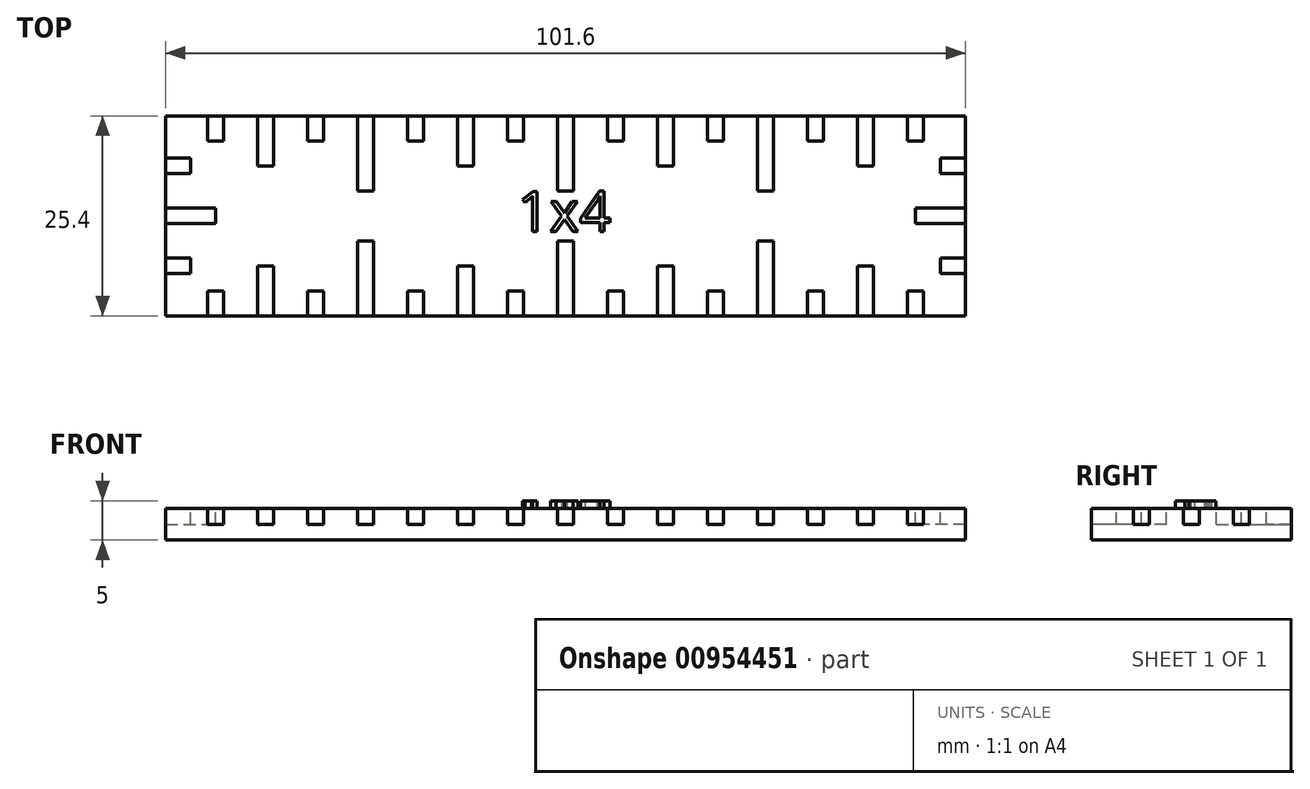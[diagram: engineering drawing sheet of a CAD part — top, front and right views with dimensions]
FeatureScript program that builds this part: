
annotation { "Feature Type Name" : "Feature", "Feature Type Description" : "" }
export const myFeature = defineFeature(function(context is Context, id is Id, definition is map)
    precondition{}
    {
        {
            var Q0;
            Q0=qCreatedBy(makeId("Top.planeOp"),FACE);
            var sketch = newSketch(context, id + "F0", { "sketchPlane" : qUnion([Q0])});
            skLineSegment(sketch, "E0.bottom", {"start": v(-50.8, 12.7) * mm, "end": v(50.8, 12.7) * mm});
            skLineSegment(sketch, "E0.top", {"start": v(-50.8, -12.7) * mm, "end": v(50.8, -12.7) * mm});
            skLineSegment(sketch, "E0.left", {"start": v(-50.8, 12.7) * mm, "end": v(-50.8, -12.7) * mm});
            skLineSegment(sketch, "E0.right", {"start": v(50.8, 12.7) * mm, "end": v(50.8, -12.7) * mm});
            skPoint(sketch, "E0.middle", {"position": v(0, 0) * mm});
            skSolve(sketch);
        }
        {
            var Q0;
            Q0=makeQuery(id+"F0.imprint","IMPRINT",FACE,{"disambiguationData":[TD([[makeQuery(id+"F0.imprint","IMPRINT",EDGE,{"derivedFrom":sQuery(id+"F0.wireOp",EDGE,"E0.bottom")}),-1.0]])]});
            extrude(context, id + "F1", {"entities" : qUnion([Q0]), "depth" : 4 * mm, "offsetDistance" : 25 * mm});
        }
        {
            var Q0;
            Q0=makeQuery(id+"F1.opExtrude","CAP_FACE",FACE,{"disambiguationData":[OSD([sQuery(id+"F0.wireOp",EDGE,"E0.bottom"),sQuery(id+"F0.wireOp",EDGE,"E0.top"),sQuery(id+"F0.wireOp",EDGE,"E0.left"),sQuery(id+"F0.wireOp",EDGE,"E0.right")])],"isStart":false});
            var sketch = newSketch(context, id + "F2", { "sketchPlane" : qUnion([Q0])});
            skLineSegment(sketch, "E1.bottom", {"start": v(-1, -3.17) * mm, "end": v(1, -3.17) * mm});
            skLineSegment(sketch, "E1.top", {"start": v(-1, -22.23) * mm, "end": v(1, -22.23) * mm});
            skLineSegment(sketch, "E1.left", {"start": v(-1, -3.17) * mm, "end": v(-1, -22.23) * mm});
            skLineSegment(sketch, "E1.right", {"start": v(1, -3.17) * mm, "end": v(1, -22.23) * mm});
            skPoint(sketch, "E1.middle", {"position": v(0, -12.7) * mm});
            skLineSegment(sketch, "E2.bottom", {"start": v(5.35, -9.53) * mm, "end": v(7.35, -9.53) * mm});
            skLineSegment(sketch, "E2.top", {"start": v(5.35, -15.88) * mm, "end": v(7.35, -15.88) * mm});
            skLineSegment(sketch, "E2.left", {"start": v(5.35, -9.53) * mm, "end": v(5.35, -15.88) * mm});
            skLineSegment(sketch, "E2.right", {"start": v(7.35, -9.53) * mm, "end": v(7.35, -15.88) * mm});
            skPoint(sketch, "E2.middle", {"position": v(6.35, -12.7) * mm});
            skLineSegment(sketch, "E3.bottom", {"start": v(-7.35, -9.53) * mm, "end": v(-5.35, -9.53) * mm});
            skLineSegment(sketch, "E3.top", {"start": v(-7.35, -15.88) * mm, "end": v(-5.35, -15.88) * mm});
            skLineSegment(sketch, "E3.left", {"start": v(-7.35, -9.53) * mm, "end": v(-7.35, -15.88) * mm});
            skLineSegment(sketch, "E3.right", {"start": v(-5.35, -9.53) * mm, "end": v(-5.35, -15.88) * mm});
            skPoint(sketch, "E3.middle", {"position": v(-6.35, -12.7) * mm});
            skLineSegment(sketch, "E4.bottom", {"start": v(-57.15, -1) * mm, "end": v(-57.15, 1) * mm});
            skLineSegment(sketch, "E4.top", {"start": v(-44.45, -1) * mm, "end": v(-44.45, 1) * mm});
            skLineSegment(sketch, "E4.left", {"start": v(-57.15, -1) * mm, "end": v(-44.45, -1) * mm});
            skLineSegment(sketch, "E4.right", {"start": v(-57.15, 1) * mm, "end": v(-44.45, 1) * mm});
            skPoint(sketch, "E4.middle", {"position": v(-50.8, 0) * mm});
            skLineSegment(sketch, "E5.bottom", {"start": v(-53.98, 5.35) * mm, "end": v(-53.98, 7.35) * mm});
            skLineSegment(sketch, "E5.top", {"start": v(-47.63, 5.35) * mm, "end": v(-47.63, 7.35) * mm});
            skLineSegment(sketch, "E5.left", {"start": v(-53.98, 5.35) * mm, "end": v(-47.63, 5.35) * mm});
            skLineSegment(sketch, "E5.right", {"start": v(-53.98, 7.35) * mm, "end": v(-47.63, 7.35) * mm});
            skPoint(sketch, "E5.middle", {"position": v(-50.8, 6.35) * mm});
            skLineSegment(sketch, "E6.bottom", {"start": v(-53.98, -7.35) * mm, "end": v(-53.98, -5.35) * mm});
            skLineSegment(sketch, "E6.top", {"start": v(-47.63, -7.35) * mm, "end": v(-47.63, -5.35) * mm});
            skLineSegment(sketch, "E6.left", {"start": v(-53.98, -7.35) * mm, "end": v(-47.63, -7.35) * mm});
            skLineSegment(sketch, "E6.right", {"start": v(-53.98, -5.35) * mm, "end": v(-47.63, -5.35) * mm});
            skPoint(sketch, "E6.middle", {"position": v(-50.8, -6.35) * mm});
            skLineSegment(sketch, "E7.bottom", {"start": v(1, 3.17) * mm, "end": v(-1, 3.17) * mm});
            skLineSegment(sketch, "E7.top", {"start": v(1, 22.22) * mm, "end": v(-1, 22.22) * mm});
            skLineSegment(sketch, "E7.left", {"start": v(1, 3.17) * mm, "end": v(1, 22.22) * mm});
            skLineSegment(sketch, "E7.right", {"start": v(-1, 3.17) * mm, "end": v(-1, 22.22) * mm});
            skPoint(sketch, "E7.middle", {"position": v(0, 12.7) * mm});
            skLineSegment(sketch, "E8.bottom", {"start": v(-5.35, 9.53) * mm, "end": v(-7.35, 9.53) * mm});
            skLineSegment(sketch, "E8.top", {"start": v(-5.35, 15.88) * mm, "end": v(-7.35, 15.88) * mm});
            skLineSegment(sketch, "E8.left", {"start": v(-5.35, 9.53) * mm, "end": v(-5.35, 15.88) * mm});
            skLineSegment(sketch, "E8.right", {"start": v(-7.35, 9.53) * mm, "end": v(-7.35, 15.88) * mm});
            skPoint(sketch, "E8.middle", {"position": v(-6.35, 12.7) * mm});
            skLineSegment(sketch, "E9.bottom", {"start": v(7.35, 9.52) * mm, "end": v(5.35, 9.52) * mm});
            skLineSegment(sketch, "E9.top", {"start": v(7.35, 15.88) * mm, "end": v(5.35, 15.88) * mm});
            skLineSegment(sketch, "E9.left", {"start": v(7.35, 9.52) * mm, "end": v(7.35, 15.88) * mm});
            skLineSegment(sketch, "E9.right", {"start": v(5.35, 9.52) * mm, "end": v(5.35, 15.88) * mm});
            skPoint(sketch, "E9.middle", {"position": v(6.35, 12.7) * mm});
            skLineSegment(sketch, "E10.bottom", {"start": v(57.15, 1) * mm, "end": v(57.15, -1) * mm});
            skLineSegment(sketch, "E10.top", {"start": v(44.45, 1) * mm, "end": v(44.45, -1) * mm});
            skLineSegment(sketch, "E10.left", {"start": v(57.15, 1) * mm, "end": v(44.45, 1) * mm});
            skLineSegment(sketch, "E10.right", {"start": v(57.15, -1) * mm, "end": v(44.45, -1) * mm});
            skPoint(sketch, "E10.middle", {"position": v(50.8, 0) * mm});
            skLineSegment(sketch, "E11.bottom", {"start": v(53.98, -5.35) * mm, "end": v(53.98, -7.35) * mm});
            skLineSegment(sketch, "E11.top", {"start": v(47.63, -5.35) * mm, "end": v(47.63, -7.35) * mm});
            skLineSegment(sketch, "E11.left", {"start": v(53.98, -5.35) * mm, "end": v(47.63, -5.35) * mm});
            skLineSegment(sketch, "E11.right", {"start": v(53.98, -7.35) * mm, "end": v(47.63, -7.35) * mm});
            skPoint(sketch, "E11.middle", {"position": v(50.8, -6.35) * mm});
            skLineSegment(sketch, "E12.bottom", {"start": v(53.98, 7.35) * mm, "end": v(53.98, 5.35) * mm});
            skLineSegment(sketch, "E12.top", {"start": v(47.63, 7.35) * mm, "end": v(47.63, 5.35) * mm});
            skLineSegment(sketch, "E12.left", {"start": v(53.98, 7.35) * mm, "end": v(47.63, 7.35) * mm});
            skLineSegment(sketch, "E12.right", {"start": v(53.98, 5.35) * mm, "end": v(47.63, 5.35) * mm});
            skPoint(sketch, "E12.middle", {"position": v(50.8, 6.35) * mm});
            skLineSegment(sketch, "E13.bottom", {"start": v(-11.7, 6.35) * mm, "end": v(-13.7, 6.35) * mm});
            skLineSegment(sketch, "E13.top", {"start": v(-11.7, 19.05) * mm, "end": v(-13.7, 19.05) * mm});
            skLineSegment(sketch, "E13.left", {"start": v(-11.7, 6.35) * mm, "end": v(-11.7, 19.05) * mm});
            skLineSegment(sketch, "E13.right", {"start": v(-13.7, 6.35) * mm, "end": v(-13.7, 19.05) * mm});
            skPoint(sketch, "E13.middle", {"position": v(-12.7, 12.7) * mm});
            skLineSegment(sketch, "E14.bottom", {"start": v(-18.05, 9.53) * mm, "end": v(-20.05, 9.53) * mm});
            skLineSegment(sketch, "E14.top", {"start": v(-18.05, 15.88) * mm, "end": v(-20.05, 15.88) * mm});
            skLineSegment(sketch, "E14.left", {"start": v(-18.05, 9.53) * mm, "end": v(-18.05, 15.88) * mm});
            skLineSegment(sketch, "E14.right", {"start": v(-20.05, 9.53) * mm, "end": v(-20.05, 15.88) * mm});
            skPoint(sketch, "E14.middle", {"position": v(-19.05, 12.7) * mm});
            skLineSegment(sketch, "E15.bottom", {"start": v(-11.7, -19.05) * mm, "end": v(-13.7, -19.05) * mm});
            skLineSegment(sketch, "E15.top", {"start": v(-11.7, -6.35) * mm, "end": v(-13.7, -6.35) * mm});
            skLineSegment(sketch, "E15.left", {"start": v(-11.7, -19.05) * mm, "end": v(-11.7, -6.35) * mm});
            skLineSegment(sketch, "E15.right", {"start": v(-13.7, -19.05) * mm, "end": v(-13.7, -6.35) * mm});
            skPoint(sketch, "E15.middle", {"position": v(-12.7, -12.7) * mm});
            skLineSegment(sketch, "E16.bottom", {"start": v(-18.05, -15.88) * mm, "end": v(-20.05, -15.88) * mm});
            skLineSegment(sketch, "E16.top", {"start": v(-18.05, -9.53) * mm, "end": v(-20.05, -9.53) * mm});
            skLineSegment(sketch, "E16.left", {"start": v(-18.05, -15.88) * mm, "end": v(-18.05, -9.53) * mm});
            skLineSegment(sketch, "E16.right", {"start": v(-20.05, -15.88) * mm, "end": v(-20.05, -9.53) * mm});
            skPoint(sketch, "E16.middle", {"position": v(-19.05, -12.7) * mm});
            skLineSegment(sketch, "E17.bottom", {"start": v(-5.35, -15.88) * mm, "end": v(-7.35, -15.88) * mm});
            skLineSegment(sketch, "E17.top", {"start": v(-5.35, -9.53) * mm, "end": v(-7.35, -9.53) * mm});
            skLineSegment(sketch, "E17.left", {"start": v(-5.35, -15.88) * mm, "end": v(-5.35, -9.53) * mm});
            skLineSegment(sketch, "E17.right", {"start": v(-7.35, -15.88) * mm, "end": v(-7.35, -9.53) * mm});
            skLineSegment(sketch, "E18.bottom", {"start": v(11.7, -6.35) * mm, "end": v(13.7, -6.35) * mm});
            skLineSegment(sketch, "E18.top", {"start": v(11.7, -19.05) * mm, "end": v(13.7, -19.05) * mm});
            skLineSegment(sketch, "E18.left", {"start": v(11.7, -6.35) * mm, "end": v(11.7, -19.05) * mm});
            skLineSegment(sketch, "E18.right", {"start": v(13.7, -6.35) * mm, "end": v(13.7, -19.05) * mm});
            skPoint(sketch, "E18.middle", {"position": v(12.7, -12.7) * mm});
            skLineSegment(sketch, "E19.bottom", {"start": v(18.05, -9.53) * mm, "end": v(20.05, -9.53) * mm});
            skLineSegment(sketch, "E19.top", {"start": v(18.05, -15.88) * mm, "end": v(20.05, -15.88) * mm});
            skLineSegment(sketch, "E19.left", {"start": v(18.05, -9.53) * mm, "end": v(18.05, -15.88) * mm});
            skLineSegment(sketch, "E19.right", {"start": v(20.05, -9.53) * mm, "end": v(20.05, -15.88) * mm});
            skPoint(sketch, "E19.middle", {"position": v(19.05, -12.7) * mm});
            skLineSegment(sketch, "E20.bottom", {"start": v(11.7, 19.05) * mm, "end": v(13.7, 19.05) * mm});
            skLineSegment(sketch, "E20.top", {"start": v(11.7, 6.35) * mm, "end": v(13.7, 6.35) * mm});
            skLineSegment(sketch, "E20.left", {"start": v(11.7, 19.05) * mm, "end": v(11.7, 6.35) * mm});
            skLineSegment(sketch, "E20.right", {"start": v(13.7, 19.05) * mm, "end": v(13.7, 6.35) * mm});
            skPoint(sketch, "E20.middle", {"position": v(12.7, 12.7) * mm});
            skLineSegment(sketch, "E21.bottom", {"start": v(18.05, 15.88) * mm, "end": v(20.05, 15.88) * mm});
            skLineSegment(sketch, "E21.top", {"start": v(18.05, 9.53) * mm, "end": v(20.05, 9.53) * mm});
            skLineSegment(sketch, "E21.left", {"start": v(18.05, 15.88) * mm, "end": v(18.05, 9.53) * mm});
            skLineSegment(sketch, "E21.right", {"start": v(20.05, 15.88) * mm, "end": v(20.05, 9.53) * mm});
            skPoint(sketch, "E21.middle", {"position": v(19.05, 12.7) * mm});
            skLineSegment(sketch, "E22.bottom", {"start": v(5.35, 15.88) * mm, "end": v(7.35, 15.88) * mm});
            skLineSegment(sketch, "E22.top", {"start": v(5.35, 9.53) * mm, "end": v(7.35, 9.53) * mm});
            skLineSegment(sketch, "E22.left", {"start": v(5.35, 15.88) * mm, "end": v(5.35, 9.53) * mm});
            skLineSegment(sketch, "E22.right", {"start": v(7.35, 15.88) * mm, "end": v(7.35, 9.53) * mm});
            skLineSegment(sketch, "E23.bottom", {"start": v(26.4, 3.17) * mm, "end": v(24.4, 3.17) * mm});
            skLineSegment(sketch, "E23.top", {"start": v(26.4, 22.22) * mm, "end": v(24.4, 22.22) * mm});
            skLineSegment(sketch, "E23.left", {"start": v(26.4, 3.17) * mm, "end": v(26.4, 22.22) * mm});
            skLineSegment(sketch, "E23.right", {"start": v(24.4, 3.17) * mm, "end": v(24.4, 22.22) * mm});
            skPoint(sketch, "E23.middle", {"position": v(25.4, 12.7) * mm});
            skLineSegment(sketch, "E24.bottom", {"start": v(20.05, 9.52) * mm, "end": v(18.05, 9.52) * mm});
            skLineSegment(sketch, "E24.top", {"start": v(20.05, 15.87) * mm, "end": v(18.05, 15.87) * mm});
            skLineSegment(sketch, "E24.left", {"start": v(20.05, 9.52) * mm, "end": v(20.05, 15.87) * mm});
            skLineSegment(sketch, "E24.right", {"start": v(18.05, 9.52) * mm, "end": v(18.05, 15.87) * mm});
            skLineSegment(sketch, "E25.bottom", {"start": v(32.75, 9.52) * mm, "end": v(30.75, 9.52) * mm});
            skLineSegment(sketch, "E25.top", {"start": v(32.75, 15.87) * mm, "end": v(30.75, 15.87) * mm});
            skLineSegment(sketch, "E25.left", {"start": v(32.75, 9.52) * mm, "end": v(32.75, 15.87) * mm});
            skLineSegment(sketch, "E25.right", {"start": v(30.75, 9.52) * mm, "end": v(30.75, 15.87) * mm});
            skPoint(sketch, "E25.middle", {"position": v(31.75, 12.7) * mm});
            skLineSegment(sketch, "E26.bottom", {"start": v(20.05, 9.53) * mm, "end": v(18.05, 9.53) * mm});
            skLineSegment(sketch, "E26.top", {"start": v(20.05, 15.88) * mm, "end": v(18.05, 15.88) * mm});
            skLineSegment(sketch, "E26.left", {"start": v(20.05, 9.53) * mm, "end": v(20.05, 15.88) * mm});
            skLineSegment(sketch, "E26.right", {"start": v(18.05, 9.53) * mm, "end": v(18.05, 15.88) * mm});
            skLineSegment(sketch, "E27.bottom", {"start": v(37.1, 19.05) * mm, "end": v(39.1, 19.05) * mm});
            skLineSegment(sketch, "E27.top", {"start": v(37.1, 6.35) * mm, "end": v(39.1, 6.35) * mm});
            skLineSegment(sketch, "E27.left", {"start": v(37.1, 19.05) * mm, "end": v(37.1, 6.35) * mm});
            skLineSegment(sketch, "E27.right", {"start": v(39.1, 19.05) * mm, "end": v(39.1, 6.35) * mm});
            skPoint(sketch, "E27.middle", {"position": v(38.1, 12.7) * mm});
            skLineSegment(sketch, "E28.bottom", {"start": v(43.45, 15.87) * mm, "end": v(45.45, 15.87) * mm});
            skLineSegment(sketch, "E28.top", {"start": v(43.45, 9.52) * mm, "end": v(45.45, 9.52) * mm});
            skLineSegment(sketch, "E28.left", {"start": v(43.45, 15.87) * mm, "end": v(43.45, 9.52) * mm});
            skLineSegment(sketch, "E28.right", {"start": v(45.45, 15.87) * mm, "end": v(45.45, 9.52) * mm});
            skPoint(sketch, "E28.middle", {"position": v(44.45, 12.7) * mm});
            skLineSegment(sketch, "E29.bottom", {"start": v(30.75, 15.87) * mm, "end": v(32.75, 15.87) * mm});
            skLineSegment(sketch, "E29.top", {"start": v(30.75, 9.52) * mm, "end": v(32.75, 9.52) * mm});
            skLineSegment(sketch, "E29.left", {"start": v(30.75, 15.87) * mm, "end": v(30.75, 9.52) * mm});
            skLineSegment(sketch, "E29.right", {"start": v(32.75, 15.87) * mm, "end": v(32.75, 9.52) * mm});
            skLineSegment(sketch, "E30.bottom", {"start": v(26.4, -22.22) * mm, "end": v(24.4, -22.22) * mm});
            skLineSegment(sketch, "E30.top", {"start": v(26.4, -3.17) * mm, "end": v(24.4, -3.17) * mm});
            skLineSegment(sketch, "E30.left", {"start": v(26.4, -22.22) * mm, "end": v(26.4, -3.17) * mm});
            skLineSegment(sketch, "E30.right", {"start": v(24.4, -22.22) * mm, "end": v(24.4, -3.17) * mm});
            skPoint(sketch, "E30.middle", {"position": v(25.4, -12.7) * mm});
            skLineSegment(sketch, "E31.bottom", {"start": v(20.05, -15.87) * mm, "end": v(18.05, -15.87) * mm});
            skLineSegment(sketch, "E31.top", {"start": v(20.05, -9.52) * mm, "end": v(18.05, -9.52) * mm});
            skLineSegment(sketch, "E31.left", {"start": v(20.05, -15.87) * mm, "end": v(20.05, -9.52) * mm});
            skLineSegment(sketch, "E31.right", {"start": v(18.05, -15.87) * mm, "end": v(18.05, -9.52) * mm});
            skLineSegment(sketch, "E32.bottom", {"start": v(32.75, -15.87) * mm, "end": v(30.75, -15.87) * mm});
            skLineSegment(sketch, "E32.top", {"start": v(32.75, -9.52) * mm, "end": v(30.75, -9.52) * mm});
            skLineSegment(sketch, "E32.left", {"start": v(32.75, -15.87) * mm, "end": v(32.75, -9.52) * mm});
            skLineSegment(sketch, "E32.right", {"start": v(30.75, -15.87) * mm, "end": v(30.75, -9.52) * mm});
            skPoint(sketch, "E32.middle", {"position": v(31.75, -12.7) * mm});
            skLineSegment(sketch, "E33.bottom", {"start": v(37.1, -6.35) * mm, "end": v(39.1, -6.35) * mm});
            skLineSegment(sketch, "E33.top", {"start": v(37.1, -19.05) * mm, "end": v(39.1, -19.05) * mm});
            skLineSegment(sketch, "E33.left", {"start": v(37.1, -6.35) * mm, "end": v(37.1, -19.05) * mm});
            skLineSegment(sketch, "E33.right", {"start": v(39.1, -6.35) * mm, "end": v(39.1, -19.05) * mm});
            skPoint(sketch, "E33.middle", {"position": v(38.1, -12.7) * mm});
            skLineSegment(sketch, "E34.bottom", {"start": v(43.45, -9.52) * mm, "end": v(45.45, -9.52) * mm});
            skLineSegment(sketch, "E34.top", {"start": v(43.45, -15.87) * mm, "end": v(45.45, -15.87) * mm});
            skLineSegment(sketch, "E34.left", {"start": v(43.45, -9.52) * mm, "end": v(43.45, -15.87) * mm});
            skLineSegment(sketch, "E34.right", {"start": v(45.45, -9.52) * mm, "end": v(45.45, -15.87) * mm});
            skPoint(sketch, "E34.middle", {"position": v(44.45, -12.7) * mm});
            skLineSegment(sketch, "E35.bottom", {"start": v(30.75, -9.52) * mm, "end": v(32.75, -9.52) * mm});
            skLineSegment(sketch, "E35.top", {"start": v(30.75, -15.87) * mm, "end": v(32.75, -15.87) * mm});
            skLineSegment(sketch, "E35.left", {"start": v(30.75, -9.52) * mm, "end": v(30.75, -15.87) * mm});
            skLineSegment(sketch, "E35.right", {"start": v(32.75, -9.52) * mm, "end": v(32.75, -15.87) * mm});
            skLineSegment(sketch, "E36.bottom", {"start": v(-26.4, -3.17) * mm, "end": v(-24.4, -3.17) * mm});
            skLineSegment(sketch, "E36.top", {"start": v(-26.4, -22.22) * mm, "end": v(-24.4, -22.22) * mm});
            skLineSegment(sketch, "E36.left", {"start": v(-26.4, -3.17) * mm, "end": v(-26.4, -22.22) * mm});
            skLineSegment(sketch, "E36.right", {"start": v(-24.4, -3.17) * mm, "end": v(-24.4, -22.22) * mm});
            skPoint(sketch, "E36.middle", {"position": v(-25.4, -12.7) * mm});
            skLineSegment(sketch, "E37.bottom", {"start": v(-20.05, -9.52) * mm, "end": v(-18.05, -9.52) * mm});
            skLineSegment(sketch, "E37.top", {"start": v(-20.05, -15.87) * mm, "end": v(-18.05, -15.87) * mm});
            skLineSegment(sketch, "E37.left", {"start": v(-20.05, -9.52) * mm, "end": v(-20.05, -15.87) * mm});
            skLineSegment(sketch, "E37.right", {"start": v(-18.05, -9.52) * mm, "end": v(-18.05, -15.87) * mm});
            skLineSegment(sketch, "E38.bottom", {"start": v(-32.75, -9.52) * mm, "end": v(-30.75, -9.52) * mm});
            skLineSegment(sketch, "E38.top", {"start": v(-32.75, -15.87) * mm, "end": v(-30.75, -15.87) * mm});
            skLineSegment(sketch, "E38.left", {"start": v(-32.75, -9.52) * mm, "end": v(-32.75, -15.87) * mm});
            skLineSegment(sketch, "E38.right", {"start": v(-30.75, -9.52) * mm, "end": v(-30.75, -15.87) * mm});
            skPoint(sketch, "E38.middle", {"position": v(-31.75, -12.7) * mm});
            skLineSegment(sketch, "E39.bottom", {"start": v(-20.05, -9.53) * mm, "end": v(-18.05, -9.53) * mm});
            skLineSegment(sketch, "E39.top", {"start": v(-20.05, -15.88) * mm, "end": v(-18.05, -15.88) * mm});
            skLineSegment(sketch, "E39.left", {"start": v(-20.05, -9.53) * mm, "end": v(-20.05, -15.88) * mm});
            skLineSegment(sketch, "E39.right", {"start": v(-18.05, -9.53) * mm, "end": v(-18.05, -15.88) * mm});
            skLineSegment(sketch, "E40.bottom", {"start": v(-37.1, -19.05) * mm, "end": v(-39.1, -19.05) * mm});
            skLineSegment(sketch, "E40.top", {"start": v(-37.1, -6.35) * mm, "end": v(-39.1, -6.35) * mm});
            skLineSegment(sketch, "E40.left", {"start": v(-37.1, -19.05) * mm, "end": v(-37.1, -6.35) * mm});
            skLineSegment(sketch, "E40.right", {"start": v(-39.1, -19.05) * mm, "end": v(-39.1, -6.35) * mm});
            skPoint(sketch, "E40.middle", {"position": v(-38.1, -12.7) * mm});
            skLineSegment(sketch, "E41.bottom", {"start": v(-43.45, -15.87) * mm, "end": v(-45.45, -15.87) * mm});
            skLineSegment(sketch, "E41.top", {"start": v(-43.45, -9.52) * mm, "end": v(-45.45, -9.52) * mm});
            skLineSegment(sketch, "E41.left", {"start": v(-43.45, -15.87) * mm, "end": v(-43.45, -9.52) * mm});
            skLineSegment(sketch, "E41.right", {"start": v(-45.45, -15.87) * mm, "end": v(-45.45, -9.52) * mm});
            skPoint(sketch, "E41.middle", {"position": v(-44.45, -12.7) * mm});
            skLineSegment(sketch, "E42.bottom", {"start": v(-30.75, -15.87) * mm, "end": v(-32.75, -15.87) * mm});
            skLineSegment(sketch, "E42.top", {"start": v(-30.75, -9.52) * mm, "end": v(-32.75, -9.52) * mm});
            skLineSegment(sketch, "E42.left", {"start": v(-30.75, -15.87) * mm, "end": v(-30.75, -9.52) * mm});
            skLineSegment(sketch, "E42.right", {"start": v(-32.75, -15.87) * mm, "end": v(-32.75, -9.52) * mm});
            skLineSegment(sketch, "E43.bottom", {"start": v(-26.4, 22.22) * mm, "end": v(-24.4, 22.22) * mm});
            skLineSegment(sketch, "E43.top", {"start": v(-26.4, 3.17) * mm, "end": v(-24.4, 3.17) * mm});
            skLineSegment(sketch, "E43.left", {"start": v(-26.4, 22.22) * mm, "end": v(-26.4, 3.17) * mm});
            skLineSegment(sketch, "E43.right", {"start": v(-24.4, 22.22) * mm, "end": v(-24.4, 3.17) * mm});
            skPoint(sketch, "E43.middle", {"position": v(-25.4, 12.7) * mm});
            skLineSegment(sketch, "E44.bottom", {"start": v(-20.05, 15.87) * mm, "end": v(-18.05, 15.87) * mm});
            skLineSegment(sketch, "E44.top", {"start": v(-20.05, 9.52) * mm, "end": v(-18.05, 9.52) * mm});
            skLineSegment(sketch, "E44.left", {"start": v(-20.05, 15.87) * mm, "end": v(-20.05, 9.52) * mm});
            skLineSegment(sketch, "E44.right", {"start": v(-18.05, 15.87) * mm, "end": v(-18.05, 9.52) * mm});
            skLineSegment(sketch, "E45.bottom", {"start": v(-32.75, 15.87) * mm, "end": v(-30.75, 15.87) * mm});
            skLineSegment(sketch, "E45.top", {"start": v(-32.75, 9.52) * mm, "end": v(-30.75, 9.52) * mm});
            skLineSegment(sketch, "E45.left", {"start": v(-32.75, 15.87) * mm, "end": v(-32.75, 9.52) * mm});
            skLineSegment(sketch, "E45.right", {"start": v(-30.75, 15.87) * mm, "end": v(-30.75, 9.52) * mm});
            skPoint(sketch, "E45.middle", {"position": v(-31.75, 12.7) * mm});
            skLineSegment(sketch, "E46.bottom", {"start": v(-37.1, 6.35) * mm, "end": v(-39.1, 6.35) * mm});
            skLineSegment(sketch, "E46.top", {"start": v(-37.1, 19.05) * mm, "end": v(-39.1, 19.05) * mm});
            skLineSegment(sketch, "E46.left", {"start": v(-37.1, 6.35) * mm, "end": v(-37.1, 19.05) * mm});
            skLineSegment(sketch, "E46.right", {"start": v(-39.1, 6.35) * mm, "end": v(-39.1, 19.05) * mm});
            skPoint(sketch, "E46.middle", {"position": v(-38.1, 12.7) * mm});
            skLineSegment(sketch, "E47.bottom", {"start": v(-43.45, 9.52) * mm, "end": v(-45.45, 9.52) * mm});
            skLineSegment(sketch, "E47.top", {"start": v(-43.45, 15.87) * mm, "end": v(-45.45, 15.87) * mm});
            skLineSegment(sketch, "E47.left", {"start": v(-43.45, 9.52) * mm, "end": v(-43.45, 15.87) * mm});
            skLineSegment(sketch, "E47.right", {"start": v(-45.45, 9.52) * mm, "end": v(-45.45, 15.87) * mm});
            skPoint(sketch, "E47.middle", {"position": v(-44.45, 12.7) * mm});
            skLineSegment(sketch, "E48.bottom", {"start": v(-30.75, 9.52) * mm, "end": v(-32.75, 9.52) * mm});
            skLineSegment(sketch, "E48.top", {"start": v(-30.75, 15.87) * mm, "end": v(-32.75, 15.87) * mm});
            skLineSegment(sketch, "E48.left", {"start": v(-30.75, 9.52) * mm, "end": v(-30.75, 15.87) * mm});
            skLineSegment(sketch, "E48.right", {"start": v(-32.75, 9.52) * mm, "end": v(-32.75, 15.87) * mm});
            skSolve(sketch);
        }
        {
            var Q0;
            Q0=qSketchRegion(id+"F2",true);
            extrude(context, id + "F3", {"entities" : qUnion([Q0]), "operationType" : NewBodyOperationType.REMOVE, "oppositeDirection" : true, "depth" : 2 * mm, "offsetDistance" : 25 * mm});
        }
        {
            var Q0;
            Q0=makeQuery(id+"F1.opExtrude","CAP_FACE",FACE,{"disambiguationData":[OSD([sQuery(id+"F0.wireOp",EDGE,"E0.bottom"),sQuery(id+"F0.wireOp",EDGE,"E0.top"),sQuery(id+"F0.wireOp",EDGE,"E0.left"),sQuery(id+"F0.wireOp",EDGE,"E0.right")])],"isStart":false});
            var sketch = newSketch(context, id + "F4", { "sketchPlane" : qUnion([Q0])});
            skText(sketch, "E49", { "text": "1x4", "fontName": "OpenSans-Regular.ttf"});
            const initialGuessF4  = {"E49": [-0.00613, -0.00201, 1, 0, 0.00516]};
            skSetInitialGuess(sketch, initialGuessF4);
            skSolve(sketch);
        }
        {
            var Q0;
            Q0 = qSketchRegion(id + "F4", true);
            extrude(context, id + "F5", {"entities" : qUnion([Q0]), "operationType" : NewBodyOperationType.ADD, "depth" : 1 * mm, "offsetDistance" : 25 * mm});
        }
    });
